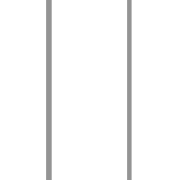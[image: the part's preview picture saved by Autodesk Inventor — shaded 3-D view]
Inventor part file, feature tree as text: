
AUTODESK INVENTOR PART (.ipt)
format: ipt  version: 2021 (Build 250183000, 183)  size: 131,072 bytes
history: native  units: in
note: dims shown in document units (in); Inventor stores cm internally (conversion verified against a paired STEP export)
features: other x4, sketch x4, plane x2, hole x1
ambient origin geometry x8: Origin, YZ Plane, XZ Plane, XY Plane, X Axis, Y Axis, Z Axis, Center Point
bodies: Solid1 (feature_tree), Body (feature_tree)
feature tree (11):
  other  "Driven Length"
  other  "Frame Generator"
  plane  "Work Plane3"
  other  "Start Plane"
  other  "End Plane"
  hole  "Hole2"  [1 undecoded]
  sketch  "Sketch"  dims[d4=2.0in d16=-0.0in d17=2.0in d18=0.12in d19=0.0in d22=1.5in d23=0.4375in d24=0.75in d25=0.635in d26=0.25in d27=0.5635in d28=1.0in d29=0.8108in d32=90.0deg d21=2.0in d8=0.5in d9=0.0344in d10=0.5in d11=0.0344in]
  sketch  "Sketch5"  dims[d0=1.5in d1=1.0in]
  sketch  "Sketch8"  dims[d2=0.0625in]
  plane  "Work Plane6"
  sketch  "Sketch9"  dims[d3=0.0625in]
note: 1 required parameter value undecoded (feature->parameter linkage not recoverable at this tier; creation-order binding heuristic only, values carry confidence <= 0.55)
